# Revit family: Windows_Purso_LK78_P50L-Facade_Single-Sash_Inward-Opening-Window-68mm
name_source: partatom
category: Windows
revit_build: Autodesk Revit 2018 (Build: 20170223_1515(x64)
units: mm (PartAtom-declared; Revit-internal decimal feet)

## family parameters
Always vertical = Yes
Cut with Voids When Loaded = No
OmniClass Number = 23.30.20.00
OmniClass Title = Windows
Room Calculation Point = No
Shared = No

## types (1)
- Windows_Purso_LK78_P50L-Facade_Single-Sash_Inward-Opening-Window-68mm
    Assembly Code = B2020100
    Description = LK78 P50L Facade Single Sash Inward Opening Window 68mm
    Edition number = 1
    Frame Material = Default
    Handle Material = Aluminium - Purso - Aluminium
    Keynote = 08500
    Leaf Material = Default
    Manufacturer = Purso
    Model = LK78 P50L Facade Single Sash Inward Opening Window 68mm
    Product Guid = bbab472f-e2b9-4b89-aa6c-1e84ce4bab91
    Product data url = https://www.bimobject.com
    URL = https://purso.fi

## geometry (parser evidence)
native form markers: Sweep x6
no freeform markers — native parametric forms only
